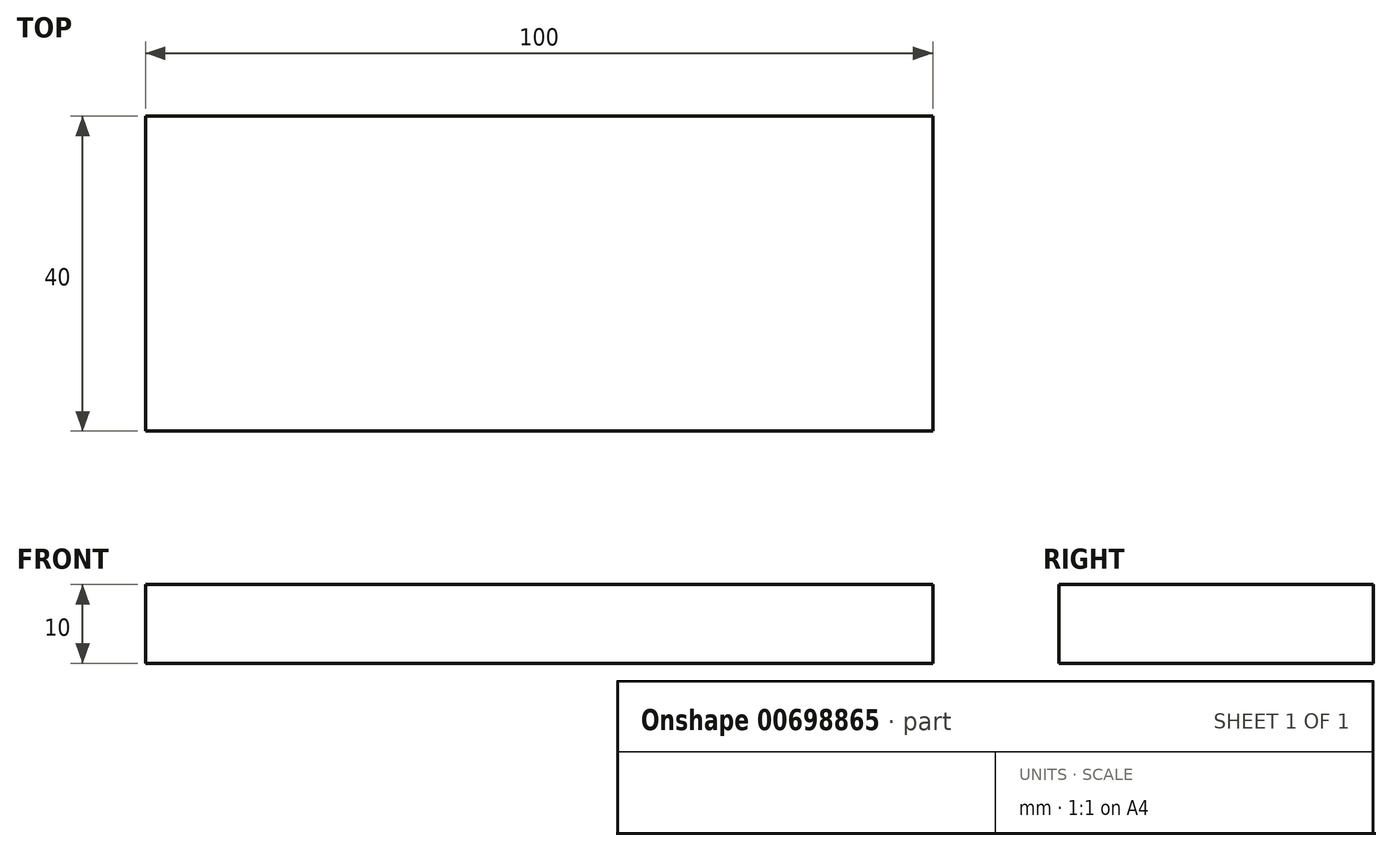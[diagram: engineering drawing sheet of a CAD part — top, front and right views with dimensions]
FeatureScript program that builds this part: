
annotation { "Feature Type Name" : "Feature", "Feature Type Description" : "" }
export const myFeature = defineFeature(function(context is Context, id is Id, definition is map)
    precondition{}
    {
        {
            var Q0;
            Q0=qCreatedBy(makeId("Top.planeOp"),FACE);
            var sketch = newSketch(context, id + "F0", { "sketchPlane" : qUnion([Q0])});
            skLineSegment(sketch, "E0.bottom", {"start": v(0, 0) * mm, "end": v(-100, 0) * mm});
            skLineSegment(sketch, "E0.top", {"start": v(0, 40) * mm, "end": v(-100, 40) * mm});
            skLineSegment(sketch, "E0.left", {"start": v(0, 0) * mm, "end": v(0, 40) * mm});
            skLineSegment(sketch, "E0.right", {"start": v(-100, 0) * mm, "end": v(-100, 40) * mm});
            skSolve(sketch);
        }
        {
            var Q0;
            Q0 = qSketchRegion(id + "F0", true);
            extrude(context, id + "F1", {"entities" : qUnion([Q0]), "depth" : 10 * mm, "offsetDistance" : 25 * mm});
        }
    });
